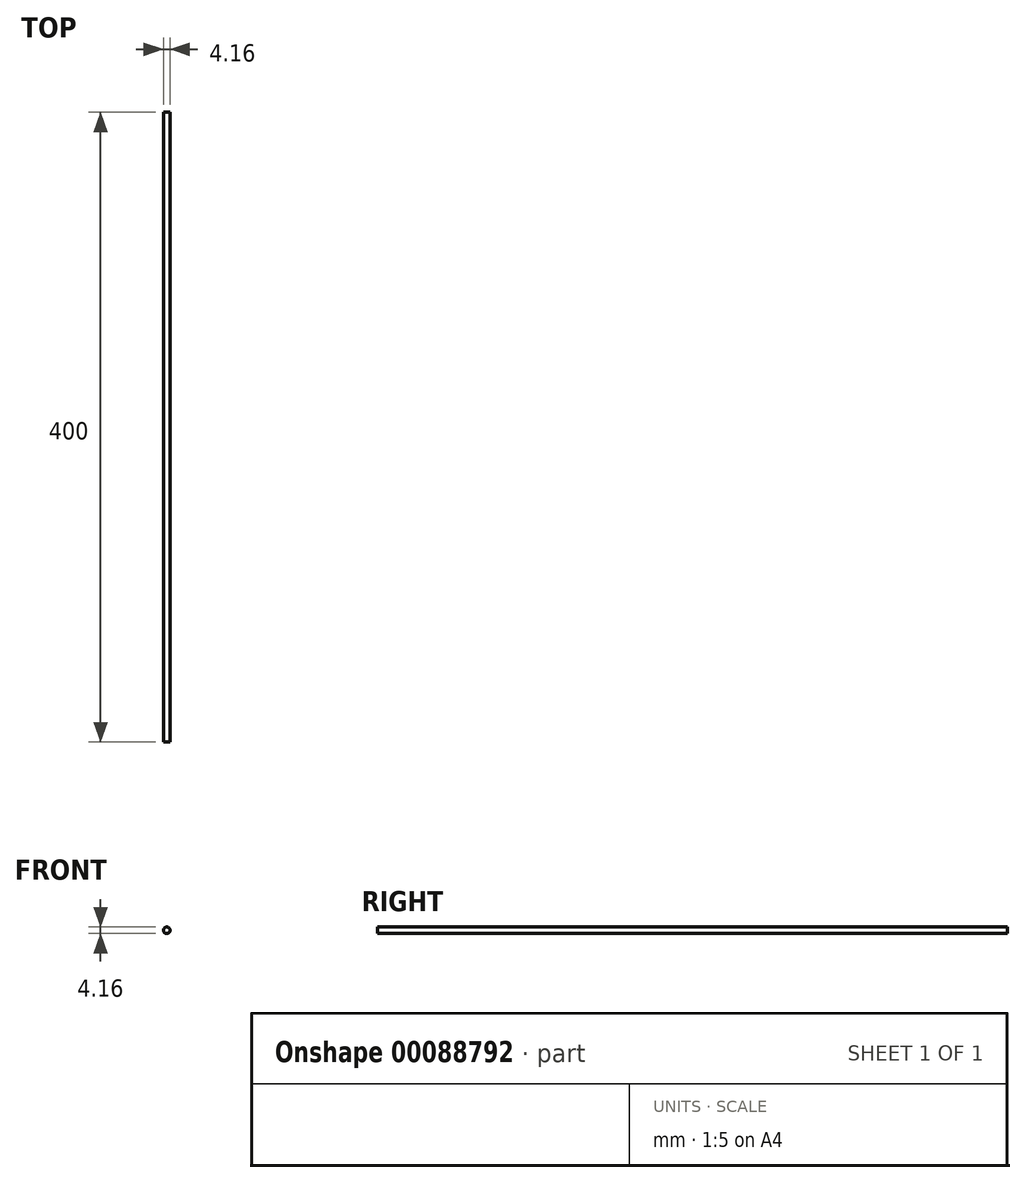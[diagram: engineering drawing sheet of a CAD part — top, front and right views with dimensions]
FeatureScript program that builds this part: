
annotation { "Feature Type Name" : "Feature", "Feature Type Description" : "" }
export const myFeature = defineFeature(function(context is Context, id is Id, definition is map)
    precondition{}
    {
        {
            var Q0;
            Q0=qCreatedBy(makeId("Front.planeOp"),FACE);
            var sketch = newSketch(context, id + "F0", { "sketchPlane" : qUnion([Q0])});
            skCircle(sketch, "E0", {"center": v(0, 0) * mm, "radius": 2.08 * mm});
            skSolve(sketch);
        }
        {
            var Q0;
            Q0 = qSketchRegion(id + "F0", true);
            extrude(context, id + "F1", {"entities" : qUnion([Q0]), "depth" : 400 * mm});
        }
    });
